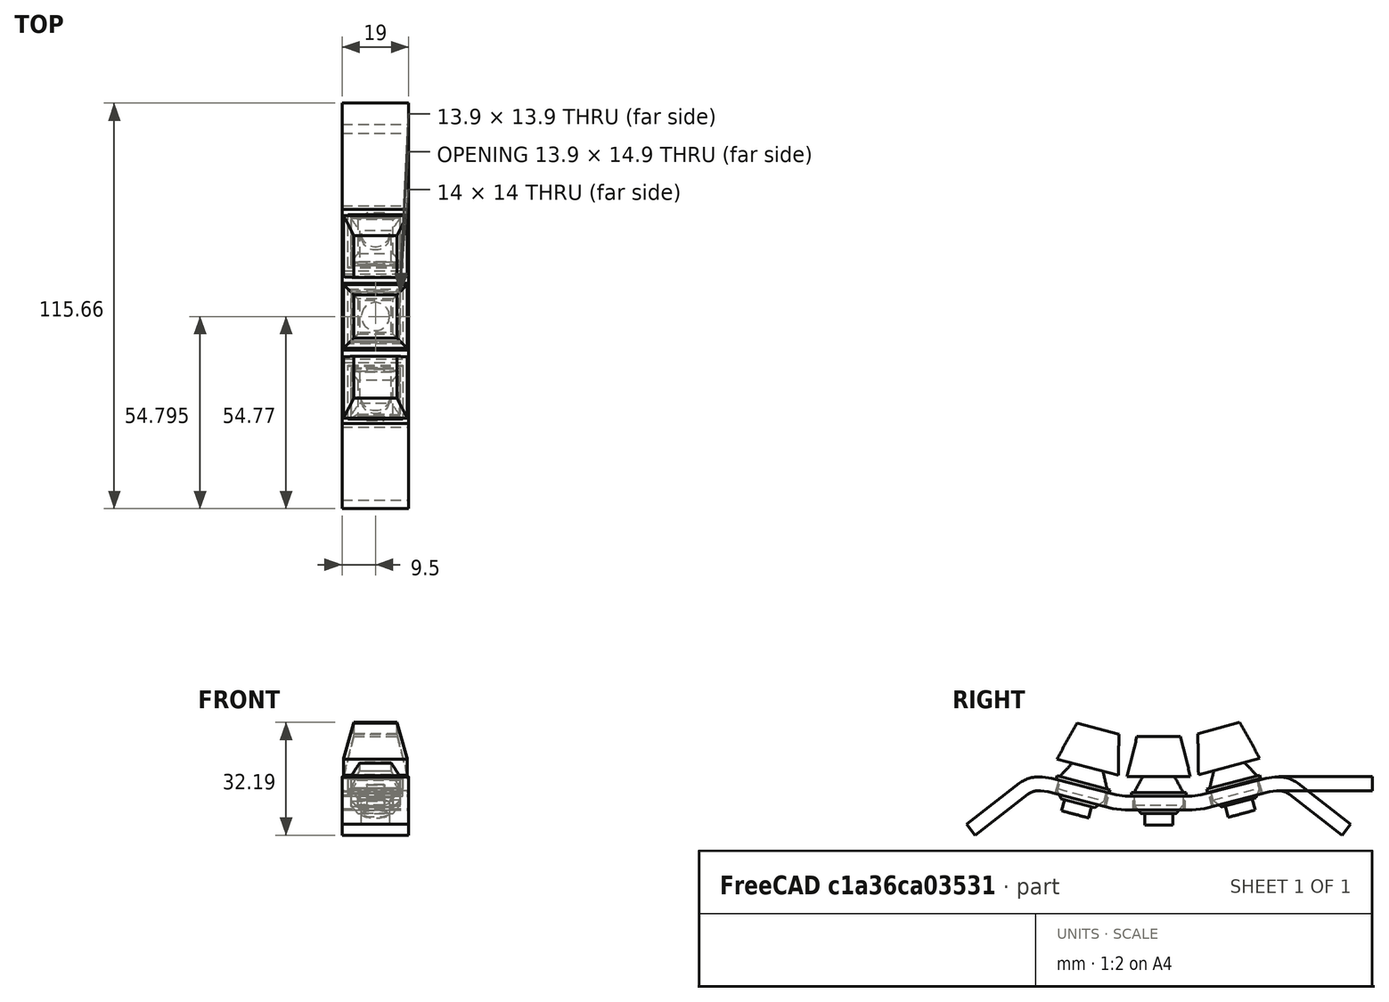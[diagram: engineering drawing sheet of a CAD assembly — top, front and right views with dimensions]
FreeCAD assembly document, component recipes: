
FREECAD ASSEMBLY — COMPONENT RECIPES ("KeyColumn")

This assembly document has 6 components, labeled P0..P5 below (a component is one placed body or linked part). 5 of them carry a construction recipe — the FreeCAD feature program that regenerates the part from scratch, quoted from this document or its linked companion documents; the rest are supplied as boundary geometry only. No exploded tour is included for this assembly.
COMPONENT P0 — recipe-attached ("KeyColumnBase", modeled in this document).
Construction recipe (the document's own serialized feature program — sketch geometry with constraints, then the solid features built on it; lengths are millimeters unless a unit is written):

FEATURE [Sketcher::SketchObject] Sketch
  FullyConstrained = true
  MapMode = 5
  Placement = pos=(0,0,0) rot=(0.57735,0.57735,0.57735;2.0944rad)
  Support = -> [YZ_Plane]
  expr: Constraints[12] = 180 - 7.25
  expr: Constraints[13] = 180 - 7.25
  expr: Constraints[16] = 180 - 7.25
  expr: Constraints[18] = 180 - 7.25
  expr: Constraints[22] = 180 - 7.25
  expr: Constraints[6] = 19.05 mm / 2
  expr: Constraints[7] = 19.05 mm / 2
  expr: Constraints[9] = 180 - 7.25
  sketch-geometry (35):
    g0: LineSegment StartX=-9.525 StartY=2 StartZ=0 EndX=9.525 EndY=2 EndZ=0
    g1: LineSegment StartX=9.525 StartY=2 StartZ=0 EndX=12.1042 EndY=2.32812 EndZ=0
    g2: LineSegment StartX=12.1042 StartY=2.32812 StartZ=0 EndX=30.5474 EndY=7.09786 EndZ=0
    g3: LineSegment StartX=30.5474 StartY=7.09786 StartZ=0 EndX=33.1266 EndY=7.42597 EndZ=0
    g4: LineSegment StartX=-9.525 StartY=2 StartZ=0 EndX=-12.1042 EndY=2.32812 EndZ=0
    g5: LineSegment StartX=-12.1042 StartY=2.32812 StartZ=0 EndX=-30.5474 EndY=7.09786 EndZ=0
    g6: ArcOfCircle CenterX=34.2584 CenterY=-1.47035 CenterZ=0 NormalX=0 NormalY=0 NormalZ=1 AngleXU=0 Radius=8.96802 StartAngle=0.911935 EndAngle=1.69733
    g7: LineSegment StartX=-30.5474 StartY=7.09786 StartZ=0 EndX=-33.1266 EndY=7.42597 EndZ=0
    g8: ArcOfCircle CenterX=-34.2584 CenterY=-1.47035 CenterZ=0 NormalX=0 NormalY=0 NormalZ=1 AngleXU=0 Radius=8.96802 StartAngle=1.44426 EndAngle=2.22966
    g9: LineSegment StartX=-31.5489 StartY=3.22527 StartZ=0 EndX=-13.1057 EndY=-1.54447 EndZ=0
    g10: LineSegment StartX=-9.525 StartY=-2 StartZ=0 EndX=9.525 EndY=-2 EndZ=0
    g11: LineSegment StartX=13.1057 StartY=-1.54447 StartZ=0 EndX=31.5489 EndY=3.22527 EndZ=0
    g12: LineSegment StartX=12.1042 StartY=2.32812 StartZ=0 EndX=13.1057 EndY=-1.54447 EndZ=0
    g13: LineSegment StartX=-13.1057 StartY=-1.54447 StartZ=0 EndX=-12.1042 EndY=2.32812 EndZ=0
    g14: LineSegment StartX=-13.1057 StartY=-1.54447 StartZ=0 EndX=-9.525 EndY=-2 EndZ=0
    g15: LineSegment StartX=9.525 StartY=-2 StartZ=0 EndX=13.1057 EndY=-1.54447 EndZ=0
    g16: LineSegment StartX=9.525 StartY=2 StartZ=0 EndX=9.525 EndY=-2 EndZ=0
    g17: LineSegment StartX=-33.1266 StartY=7.42597 StartZ=0 EndX=-33.6274 EndY=3.48968 EndZ=0
    g18: LineSegment StartX=-31.5489 StartY=3.22527 StartZ=0 EndX=-33.6274 EndY=3.48968 EndZ=0
    g19: LineSegment StartX=33.1266 StartY=7.42597 StartZ=0 EndX=33.6274 EndY=3.48968 EndZ=0
    g20: LineSegment StartX=31.5489 StartY=3.22527 StartZ=0 EndX=33.6274 EndY=3.48968 EndZ=0
    g21: ArcOfCircle CenterX=34.2584 CenterY=-1.47035 CenterZ=0 NormalX=0 NormalY=0 NormalZ=1 AngleXU=0 Radius=5 StartAngle=0.911935 EndAngle=1.69733
    g22: ArcOfCircle CenterX=-34.2584 CenterY=-1.47035 CenterZ=0 NormalX=0 NormalY=0 NormalZ=1 AngleXU=0 Radius=5 StartAngle=1.44426 EndAngle=2.22966
    g23: LineSegment StartX=-39.7488 StartY=5.62057 StartZ=0 EndX=-37.3195 EndY=2.4831 EndZ=0
    g24: LineSegment StartX=37.3195 StartY=2.4831 StartZ=0 EndX=39.7488 EndY=5.62057 EndZ=0
    g25: LineSegment StartX=33.6274 StartY=3.48968 StartZ=0 EndX=34.2584 EndY=-1.47035 EndZ=0
    g26: LineSegment StartX=37.3195 StartY=2.4831 StartZ=0 EndX=34.2584 EndY=-1.47035 EndZ=0
    g27: LineSegment StartX=-33.6274 StartY=3.48968 StartZ=0 EndX=-34.2584 EndY=-1.47035 EndZ=0
    g28: LineSegment StartX=-37.3195 StartY=2.4831 StartZ=0 EndX=-34.2584 EndY=-1.47035 EndZ=0
    g29: LineSegment StartX=37.3195 StartY=2.4831 StartZ=0 EndX=52.3426 EndY=-9.14903 EndZ=0
    g30: LineSegment StartX=52.3426 StartY=-9.14903 StartZ=0 EndX=54.7719 EndY=-6.01155 EndZ=0
    g31: LineSegment StartX=54.7719 StartY=-6.01155 StartZ=0 EndX=39.7488 EndY=5.62057 EndZ=0
    g32: LineSegment StartX=-39.7488 StartY=5.62057 StartZ=0 EndX=-54.7719 EndY=-6.01155 EndZ=0
    g33: LineSegment StartX=-54.7719 StartY=-6.01155 StartZ=0 EndX=-52.3426 EndY=-9.14903 EndZ=0
    g34: LineSegment StartX=-52.3426 StartY=-9.14903 StartZ=0 EndX=-37.3195 EndY=2.4831 EndZ=0
  constraints (94):
    c: Horizontal(g0)
    c: Coincident(g1,g0)
    c: Coincident(g3,g2)
    c: Coincident(g4,g0)
    c: Coincident(g5,g4)
    c: DistanceY(g-1,g0) = 2
    c: DistanceX(g-1,g0) = 9.525
    c: DistanceX(g0,g-1) = 9.525
    c: Distance(g1) = 2.6
    c: Angle(g1,g0) = 3.01506
    c: Coincident(g2,g1)
    c: Distance(g2) = 19.05
    c: Angle(g2,g1) = 3.01506
    c: Angle(g0,g4) = 3.01506
    c: Distance(g4) = 2.6
    c: Distance(g5) = 19.05
    c: Angle(g4,g5) = 3.01506
    c: Distance(g3) = 2.6
    c: Angle(g2,g3) = 3.01506
    c: Coincident(g6,g3)
    c: Coincident(g7,g5)
    c: Distance(g7) = 2.6
    c: Angle(g7,g5) = 3.01506
    c: Coincident(g8,g7)
    c: Horizontal(g10)
    c: Parallel(g2,g11)
    c: Parallel(g9,g5)
    c: Equal(g5,g9)
    c: Equal(g0,g10)
    c: Equal(g2,g11)
    c: Distance(g0,g10) = 4
    c: Coincident(g12,g1)
    c: Coincident(g12,g11)
    c: Perpendicular(g11,g12)
    c: Distance(g12) = 4
    c: Coincident(g13,g9)
    c: Coincident(g13,g4)
    c: Perpendicular(g9,g13)
    c: Distance(g13) = 4
    c: Coincident(g14,g9)
    c: Coincident(g14,g10)
    c: Coincident(g15,g10)
    c: Coincident(g15,g11)
    c: Coincident(g16,g0)
    c: Coincident(g16,g10)
    c: Perpendicular(g10,g16)
    c: Coincident(g17,g7)
    c: Coincident(g18,g9)
    c: Coincident(g18,g17)
    c: Perpendicular(g18,g17)
    c: Parallel(g7,g18)
    c: Coincident(g19,g3)
    c: Coincident(g20,g11)
    c: Coincident(g20,g19)
    c: Parallel(g3,g20)
    c: Perpendicular(g19,g3)
    c: Coincident(g21,g6)
    c: Coincident(g21,g20)
    c: Coincident(g22,g8)
    c: Coincident(g22,g18)
    c: Coincident(g23,g8)
    c: Coincident(g23,g22)
    c: Coincident(g24,g21)
    c: Coincident(g24,g6)
    c: Coincident(g25,g20)
    c: Coincident(g25,g6)
    c: Coincident(g26,g21)
    c: Coincident(g26,g6)
    c: Parallel(g26,g24)
    c: Parallel(g19,g25)
    c: Coincident(g27,g18)
    c: Coincident(g27,g8)
    c: Coincident(g28,g22)
    c: Coincident(g28,g8)
    c: Parallel(g23,g28)
    c: Parallel(g27,g17)
    c: Distance(g28) = 5
    c: Distance(g26) = 5
    c: Angle(g27,g28) = 0.785398
    c: Angle(g26,g25) = 0.785398
    c: Tangent(g21,g29) = 1.5708
    c: Coincident(g29,g30)
    c: Coincident(g30,g31)
    c: Coincident(g31,g6)
    c: Tangent(g8,g32) = -1.5708
    c: Coincident(g32,g33)
    c: Coincident(g33,g34)
    c: Coincident(g34,g22)
    c: Perpendicular(g33,g32)
    c: Perpendicular(g34,g33)
    c: Perpendicular(g29,g30)
    c: Perpendicular(g31,g30)
    c: Distance(g31) = 19
    c: Distance(g32) = 19
FEATURE [PartDesign::Pad] Pad
  Direction = (1,-2e-16,3e-16)
  Length = 19
  Length2 = 10
  Midplane = true
  Placement = pos=(0,0,0) rot=(1,1,1;2.0944rad)
  Profile = -> Sketch
  ReferenceAxis = -> Sketch [N_Axis]
  Type = 0
FEATURE [PartDesign::Body] Body  label="KeyColumnBase"
  Group = -> [Sketch,Pad]
  Origin = -> Origin
  Tip = -> Pad
COMPONENT P1 — recipe-attached ("SubtractorTop", modeled in this document).
Construction recipe (the document's own serialized feature program — sketch geometry with constraints, then the solid features built on it; lengths are millimeters unless a unit is written):

FEATURE [Sketcher::SketchObject] Sketch001
  FullyConstrained = true
  MapMode = 5
  Placement = pos=(0.025,21.3016,4.70673) rot=(0.125206,0.125206,-0.984199;1.58672rad)
  Support = -> [Local_CS]
  sketch-geometry (4):
    g0: LineSegment StartX=-6.95 StartY=6.95 StartZ=0 EndX=6.95 EndY=6.95 EndZ=0
    g1: LineSegment StartX=6.95 StartY=6.95 StartZ=0 EndX=6.95 EndY=-6.95 EndZ=0
    g2: LineSegment StartX=6.95 StartY=-6.95 StartZ=0 EndX=-6.95 EndY=-6.95 EndZ=0
    g3: LineSegment StartX=-6.95 StartY=-6.95 StartZ=0 EndX=-6.95 EndY=6.95 EndZ=0
  constraints (11):
    c: Coincident(g0,g1)
    c: Coincident(g1,g2)
    c: Coincident(g2,g3)
    c: Coincident(g3,g0)
    c: Horizontal(g0)
    c: Horizontal(g2)
    c: Vertical(g1)
    c: Vertical(g3)
    c: Symmetric(g0,g1,g-1)
    c: Equal(g0,g3)
    c: DistanceX(g0,g0) = 13.9
FEATURE [PartDesign::Pad] Pad001
  Direction = (-5e-16,-0.25038,0.968148)
  Length = 10
  Length2 = 10
  Placement = pos=(0.025,21.3016,4.70673) rot=(0.125206,0.125206,-0.984199;1.58672rad)
  Profile = -> Sketch001
  ReferenceAxis = -> Sketch001 [N_Axis]
  Type = 0
FEATURE [Sketcher::SketchObject] Sketch002
  ExternalGeometry = -> [Pad001]
  FullyConstrained = true
  MapMode = 5
  Placement = pos=(0.025,21.3016,4.70673) rot=(-0.704263,0.704263,0.089594;2.96288rad)
  Support = -> [Pad001]
  sketch-geometry (4):
    g0: LineSegment StartX=-6.95 StartY=6.95 StartZ=0 EndX=6.95 EndY=6.95 EndZ=0
    g1: LineSegment StartX=6.95 StartY=6.95 StartZ=0 EndX=6.95 EndY=-6.95 EndZ=0
    g2: LineSegment StartX=6.95 StartY=-6.95 StartZ=0 EndX=-6.95 EndY=-6.95 EndZ=0
    g3: LineSegment StartX=-6.95 StartY=-6.95 StartZ=0 EndX=-6.95 EndY=6.95 EndZ=0
  constraints (10):
    c: Coincident(g0,g1)
    c: Coincident(g1,g2)
    c: Coincident(g2,g3)
    c: Coincident(g3,g0)
    c: Horizontal(g0)
    c: Horizontal(g2)
    c: Vertical(g1)
    c: Vertical(g3)
    c: Coincident(g0,g-3)
    c: Coincident(g1,g-4)
FEATURE [PartDesign::Pad] Pad002
  BaseFeature = -> Pad001
  Direction = (4e-16,0.25038,-0.968148)
  Length = 1.3
  Length2 = 10
  Placement = pos=(0.025,21.3016,4.70673) rot=(0.125206,0.125206,-0.984199;1.58672rad)
  Profile = -> Sketch002
  ReferenceAxis = -> Sketch002 [N_Axis]
  Type = 0
FEATURE [Sketcher::SketchObject] Sketch003
  ExternalGeometry = -> [Pad002]
  FullyConstrained = true
  MapMode = 5
  Placement = pos=(0.025,21.6271,3.44814) rot=(-0.704263,0.704263,0.089594;2.96288rad)
  Support = -> [Pad002]
  sketch-geometry (12):
    g0: LineSegment StartX=-6.95 StartY=6.95 StartZ=0 EndX=-6.95 EndY=2.5 EndZ=0
    g1: LineSegment StartX=-6.95 StartY=2.5 StartZ=0 EndX=-7.45 EndY=2.5 EndZ=0
    g2: LineSegment StartX=-7.45 StartY=2.5 StartZ=0 EndX=-7.45 EndY=-2.5 EndZ=0
    g3: LineSegment StartX=-7.45 StartY=-2.5 StartZ=0 EndX=-6.95 EndY=-2.5 EndZ=0
    g4: LineSegment StartX=-6.95 StartY=-2.5 StartZ=0 EndX=-6.95 EndY=-6.95 EndZ=0
    g5: LineSegment StartX=-6.95 StartY=-6.95 StartZ=0 EndX=6.95 EndY=-6.95 EndZ=0
    g6: LineSegment StartX=6.95 StartY=-6.95 StartZ=0 EndX=6.95 EndY=-2.5 EndZ=0
    g7: LineSegment StartX=6.95 StartY=-2.5 StartZ=0 EndX=7.45 EndY=-2.5 EndZ=0
    g8: LineSegment StartX=7.45 StartY=-2.5 StartZ=0 EndX=7.45 EndY=2.5 EndZ=0
    g9: LineSegment StartX=7.45 StartY=2.5 StartZ=0 EndX=6.95 EndY=2.5 EndZ=0
    g10: LineSegment StartX=6.95 StartY=2.5 StartZ=0 EndX=6.95 EndY=6.95 EndZ=0
    g11: LineSegment StartX=6.95 StartY=6.95 StartZ=0 EndX=-6.95 EndY=6.95 EndZ=0
  constraints (33):
    c: Coincident(g0,g-3)
    c: Vertical(g0)
    c: Coincident(g0,g1)
    c: Horizontal(g1)
    c: Coincident(g1,g2)
    c: Vertical(g2)
    c: Coincident(g2,g3)
    c: Coincident(g3,g4)
    c: Vertical(g4)
    c: Coincident(g4,g5)
    c: Coincident(g5,g-4)
    c: Horizontal(g5)
    c: Coincident(g5,g6)
    c: Vertical(g6)
    c: Coincident(g6,g7)
    c: Coincident(g7,g8)
    c: Vertical(g8)
    c: Coincident(g8,g9)
    c: Coincident(g9,g10)
    c: Vertical(g10)
    c: Coincident(g10,g11)
    c: Coincident(g11,g0)
    c: Horizontal(g11)
    c: Horizontal(g3)
    c: Horizontal(g7)
    c: Horizontal(g9)
    c: Vertical(g9,g6)
    c: DistanceX(g3,g3) = 0.5
    c: Equal(g3,g7)
    c: DistanceY(g8,g8) = 5
    c: Symmetric(g2,g8,g-1)
    c: Equal(g8,g2)
    c: Horizontal(g3,g6)
FEATURE [PartDesign::Pad] Pad003
  BaseFeature = -> Pad002
  Direction = (4e-16,0.25038,-0.968148)
  Length = 2.7
  Length2 = 10
  Placement = pos=(0.025,21.3016,4.70673) rot=(0.125206,0.125206,-0.984199;1.58672rad)
  Profile = -> Sketch003
  ReferenceAxis = -> Sketch003 [N_Axis]
  Type = 0
FEATURE [PartDesign::Pad] Pad004
  BaseFeature = -> Pad003
  Direction = (4e-16,0.25038,-0.968148)
  Length = 10
  Length2 = 10
  Placement = pos=(0.025,21.3016,4.70673) rot=(0.125206,0.125206,-0.984199;1.58672rad)
  Profile = -> Sketch003
  ReferenceAxis = -> Sketch003 [N_Axis]
  Type = 0
FEATURE [PartDesign::Body] Body001  label="SubtractorTop"
  Group = -> [Sketch001,Pad001,Sketch002,Pad002,Sketch003,Pad003,Pad004]
  Origin = -> Origin001
  Tip = -> Pad004
COMPONENT P2 — recipe-attached ("SubtractorMiddle", modeled in this document).
Construction recipe (the document's own serialized feature program — sketch geometry with constraints, then the solid features built on it; lengths are millimeters unless a unit is written):

FEATURE [Sketcher::SketchObject] Sketch005
  FullyConstrained = true
  MapMode = 5
  Placement = pos=(0,0.025,2) rot=(0,0,-1;1.5708rad)
  Support = -> [Local_CS002]
  sketch-geometry (4):
    g0: LineSegment StartX=-6.95 StartY=6.95 StartZ=0 EndX=6.95 EndY=6.95 EndZ=0
    g1: LineSegment StartX=6.95 StartY=6.95 StartZ=0 EndX=6.95 EndY=-6.95 EndZ=0
    g2: LineSegment StartX=6.95 StartY=-6.95 StartZ=0 EndX=-6.95 EndY=-6.95 EndZ=0
    g3: LineSegment StartX=-6.95 StartY=-6.95 StartZ=0 EndX=-6.95 EndY=6.95 EndZ=0
  constraints (11):
    c: Coincident(g0,g1)
    c: Coincident(g1,g2)
    c: Coincident(g2,g3)
    c: Coincident(g3,g0)
    c: Horizontal(g0)
    c: Horizontal(g2)
    c: Vertical(g1)
    c: Vertical(g3)
    c: Symmetric(g0,g1,g-1)
    c: Equal(g0,g3)
    c: DistanceX(g0,g0) = 13.9
FEATURE [PartDesign::Pad] Pad006
  Direction = (-4e-16,6e-16,1)
  Length = 10
  Length2 = 10
  Placement = pos=(0,0.025,2) rot=(0,0,-1;1.5708rad)
  Profile = -> Sketch005
  ReferenceAxis = -> Sketch005 [N_Axis]
  Type = 0
FEATURE [Sketcher::SketchObject] Sketch006
  ExternalGeometry = -> [Pad006]
  FullyConstrained = true
  MapMode = 5
  Placement = pos=(0,0.025,2) rot=(-0.707107,0.707107,0;3.14159rad)
  Support = -> [Pad006]
  sketch-geometry (4):
    g0: LineSegment StartX=-6.95 StartY=6.95 StartZ=0 EndX=6.95 EndY=6.95 EndZ=0
    g1: LineSegment StartX=6.95 StartY=6.95 StartZ=0 EndX=6.95 EndY=-6.95 EndZ=0
    g2: LineSegment StartX=6.95 StartY=-6.95 StartZ=0 EndX=-6.95 EndY=-6.95 EndZ=0
    g3: LineSegment StartX=-6.95 StartY=-6.95 StartZ=0 EndX=-6.95 EndY=6.95 EndZ=0
  constraints (10):
    c: Coincident(g0,g1)
    c: Coincident(g1,g2)
    c: Coincident(g2,g3)
    c: Coincident(g3,g0)
    c: Horizontal(g0)
    c: Horizontal(g2)
    c: Vertical(g1)
    c: Vertical(g3)
    c: Coincident(g0,g-3)
    c: Coincident(g1,g-4)
FEATURE [PartDesign::Pad] Pad007
  BaseFeature = -> Pad006
  Direction = (4e-16,-6e-16,-1)
  Length = 1.3
  Length2 = 10
  Placement = pos=(0,0.025,2) rot=(0,0,-1;1.5708rad)
  Profile = -> Sketch006
  ReferenceAxis = -> Sketch006 [N_Axis]
  Type = 0
FEATURE [Sketcher::SketchObject] Sketch007
  ExternalGeometry = -> [Pad007]
  FullyConstrained = true
  MapMode = 5
  Placement = pos=(5e-16,0.025,0.7) rot=(-0.707107,0.707107,0;3.14159rad)
  Support = -> [Pad007]
  sketch-geometry (12):
    g0: LineSegment StartX=-6.95 StartY=6.95 StartZ=0 EndX=-6.95 EndY=2.5 EndZ=0
    g1: LineSegment StartX=-6.95 StartY=2.5 StartZ=0 EndX=-7.45 EndY=2.5 EndZ=0
    g2: LineSegment StartX=-7.45 StartY=2.5 StartZ=0 EndX=-7.45 EndY=-2.5 EndZ=0
    g3: LineSegment StartX=-7.45 StartY=-2.5 StartZ=0 EndX=-6.95 EndY=-2.5 EndZ=0
    g4: LineSegment StartX=-6.95 StartY=-2.5 StartZ=0 EndX=-6.95 EndY=-6.95 EndZ=0
    g5: LineSegment StartX=-6.95 StartY=-6.95 StartZ=0 EndX=6.95 EndY=-6.95 EndZ=0
    g6: LineSegment StartX=6.95 StartY=-6.95 StartZ=0 EndX=6.95 EndY=-2.5 EndZ=0
    g7: LineSegment StartX=6.95 StartY=-2.5 StartZ=0 EndX=7.45 EndY=-2.5 EndZ=0
    g8: LineSegment StartX=7.45 StartY=-2.5 StartZ=0 EndX=7.45 EndY=2.5 EndZ=0
    g9: LineSegment StartX=7.45 StartY=2.5 StartZ=0 EndX=6.95 EndY=2.5 EndZ=0
    g10: LineSegment StartX=6.95 StartY=2.5 StartZ=0 EndX=6.95 EndY=6.95 EndZ=0
    g11: LineSegment StartX=6.95 StartY=6.95 StartZ=0 EndX=-6.95 EndY=6.95 EndZ=0
  constraints (33):
    c: Coincident(g0,g-3)
    c: Vertical(g0)
    c: Coincident(g0,g1)
    c: Horizontal(g1)
    c: Coincident(g1,g2)
    c: Vertical(g2)
    c: Coincident(g2,g3)
    c: Coincident(g3,g4)
    c: Vertical(g4)
    c: Coincident(g4,g5)
    c: Coincident(g5,g-4)
    c: Horizontal(g5)
    c: Coincident(g5,g6)
    c: Vertical(g6)
    c: Coincident(g6,g7)
    c: Coincident(g7,g8)
    c: Vertical(g8)
    c: Coincident(g8,g9)
    c: Coincident(g9,g10)
    c: Vertical(g10)
    c: Coincident(g10,g11)
    c: Coincident(g11,g0)
    c: Horizontal(g11)
    c: Horizontal(g3)
    c: Horizontal(g7)
    c: Horizontal(g9)
    c: Vertical(g9,g6)
    c: DistanceX(g3,g3) = 0.5
    c: Equal(g3,g7)
    c: DistanceY(g8,g8) = 5
    c: Symmetric(g2,g8,g-1)
    c: Equal(g8,g2)
    c: Horizontal(g3,g6)
FEATURE [PartDesign::Pad] Pad008
  BaseFeature = -> Pad007
  Direction = (4e-16,-6e-16,-1)
  Length = 2.7
  Length2 = 10
  Placement = pos=(0,0.025,2) rot=(0,0,-1;1.5708rad)
  Profile = -> Sketch007
  ReferenceAxis = -> Sketch007 [N_Axis]
  Type = 0
FEATURE [PartDesign::Pad] Pad009
  BaseFeature = -> Pad008
  Direction = (4e-16,-6e-16,-1)
  Length = 10
  Length2 = 10
  Placement = pos=(0,0.025,2) rot=(0,0,-1;1.5708rad)
  Profile = -> Sketch007
  ReferenceAxis = -> Sketch007 [N_Axis]
  Type = 0
FEATURE [PartDesign::Body] Body002  label="SubtractorMiddle"
  Group = -> [Sketch005,Pad006,Sketch006,Pad007,Sketch007,Pad008,Pad009]
  Origin = -> Origin002
  Tip = -> Pad009
COMPONENT P3 — recipe-attached ("SubtractorBottom", modeled in this document).
Construction recipe (the document's own serialized feature program — sketch geometry with constraints, then the solid features built on it; lengths are millimeters unless a unit is written):

FEATURE [Sketcher::SketchObject] Sketch009
  FullyConstrained = true
  MapMode = 5
  Placement = pos=(-5.3e-15,-21.35,4.71925) rot=(-0.125206,-0.125206,-0.984199;1.58672rad)
  Support = -> [Local_CS001]
  sketch-geometry (4):
    g0: LineSegment StartX=-6.95 StartY=6.95 StartZ=0 EndX=6.95 EndY=6.95 EndZ=0
    g1: LineSegment StartX=6.95 StartY=6.95 StartZ=0 EndX=6.95 EndY=-6.95 EndZ=0
    g2: LineSegment StartX=6.95 StartY=-6.95 StartZ=0 EndX=-6.95 EndY=-6.95 EndZ=0
    g3: LineSegment StartX=-6.95 StartY=-6.95 StartZ=0 EndX=-6.95 EndY=6.95 EndZ=0
  constraints (11):
    c: Coincident(g0,g1)
    c: Coincident(g1,g2)
    c: Coincident(g2,g3)
    c: Coincident(g3,g0)
    c: Horizontal(g0)
    c: Horizontal(g2)
    c: Vertical(g1)
    c: Vertical(g3)
    c: Symmetric(g0,g1,g-1)
    c: Equal(g0,g3)
    c: DistanceX(g0,g0) = 13.9
FEATURE [PartDesign::Pad] Pad011
  Direction = (-2e-16,0.25038,0.968148)
  Length = 10
  Length2 = 10
  Placement = pos=(-5.3e-15,-21.35,4.71925) rot=(-0.125206,-0.125206,-0.984199;1.58672rad)
  Profile = -> Sketch009
  ReferenceAxis = -> Sketch009 [N_Axis]
  Type = 0
FEATURE [Sketcher::SketchObject] Sketch010
  ExternalGeometry = -> [Pad011]
  FullyConstrained = true
  MapMode = 5
  Placement = pos=(-5.3e-15,-21.35,4.71925) rot=(-0.704263,0.704263,-0.089594;3.3203rad)
  Support = -> [Pad011]
  sketch-geometry (4):
    g0: LineSegment StartX=-6.95 StartY=6.95 StartZ=0 EndX=6.95 EndY=6.95 EndZ=0
    g1: LineSegment StartX=6.95 StartY=6.95 StartZ=0 EndX=6.95 EndY=-6.95 EndZ=0
    g2: LineSegment StartX=6.95 StartY=-6.95 StartZ=0 EndX=-6.95 EndY=-6.95 EndZ=0
    g3: LineSegment StartX=-6.95 StartY=-6.95 StartZ=0 EndX=-6.95 EndY=6.95 EndZ=0
  constraints (10):
    c: Coincident(g0,g1)
    c: Coincident(g1,g2)
    c: Coincident(g2,g3)
    c: Coincident(g3,g0)
    c: Horizontal(g0)
    c: Horizontal(g2)
    c: Vertical(g1)
    c: Vertical(g3)
    c: Coincident(g0,g-3)
    c: Coincident(g1,g-4)
FEATURE [PartDesign::Pad] Pad012
  BaseFeature = -> Pad011
  Direction = (2e-16,-0.25038,-0.968148)
  Length = 1.3
  Length2 = 10
  Placement = pos=(-5.3e-15,-21.35,4.71925) rot=(-0.125206,-0.125206,-0.984199;1.58672rad)
  Profile = -> Sketch010
  ReferenceAxis = -> Sketch010 [N_Axis]
  Type = 0
FEATURE [Sketcher::SketchObject] Sketch011
  ExternalGeometry = -> [Pad012]
  FullyConstrained = true
  MapMode = 5
  Placement = pos=(-5e-15,-21.6755,3.46065) rot=(-0.704263,0.704263,-0.089594;3.3203rad)
  Support = -> [Pad012]
  sketch-geometry (12):
    g0: LineSegment StartX=-6.95 StartY=6.95 StartZ=0 EndX=-6.95 EndY=2.5 EndZ=0
    g1: LineSegment StartX=-6.95 StartY=2.5 StartZ=0 EndX=-7.45 EndY=2.5 EndZ=0
    g2: LineSegment StartX=-7.45 StartY=2.5 StartZ=0 EndX=-7.45 EndY=-2.5 EndZ=0
    g3: LineSegment StartX=-7.45 StartY=-2.5 StartZ=0 EndX=-6.95 EndY=-2.5 EndZ=0
    g4: LineSegment StartX=-6.95 StartY=-2.5 StartZ=0 EndX=-6.95 EndY=-6.95 EndZ=0
    g5: LineSegment StartX=-6.95 StartY=-6.95 StartZ=0 EndX=6.95 EndY=-6.95 EndZ=0
    g6: LineSegment StartX=6.95 StartY=-6.95 StartZ=0 EndX=6.95 EndY=-2.5 EndZ=0
    g7: LineSegment StartX=6.95 StartY=-2.5 StartZ=0 EndX=7.45 EndY=-2.5 EndZ=0
    g8: LineSegment StartX=7.45 StartY=-2.5 StartZ=0 EndX=7.45 EndY=2.5 EndZ=0
    g9: LineSegment StartX=7.45 StartY=2.5 StartZ=0 EndX=6.95 EndY=2.5 EndZ=0
    g10: LineSegment StartX=6.95 StartY=2.5 StartZ=0 EndX=6.95 EndY=6.95 EndZ=0
    g11: LineSegment StartX=6.95 StartY=6.95 StartZ=0 EndX=-6.95 EndY=6.95 EndZ=0
  constraints (33):
    c: Coincident(g0,g-3)
    c: Vertical(g0)
    c: Coincident(g0,g1)
    c: Horizontal(g1)
    c: Coincident(g1,g2)
    c: Vertical(g2)
    c: Coincident(g2,g3)
    c: Coincident(g3,g4)
    c: Vertical(g4)
    c: Coincident(g4,g5)
    c: Coincident(g5,g-4)
    c: Horizontal(g5)
    c: Coincident(g5,g6)
    c: Vertical(g6)
    c: Coincident(g6,g7)
    c: Coincident(g7,g8)
    c: Vertical(g8)
    c: Coincident(g8,g9)
    c: Coincident(g9,g10)
    c: Vertical(g10)
    c: Coincident(g10,g11)
    c: Coincident(g11,g0)
    c: Horizontal(g11)
    c: Horizontal(g3)
    c: Horizontal(g7)
    c: Horizontal(g9)
    c: Vertical(g9,g6)
    c: DistanceX(g3,g3) = 0.5
    c: Equal(g3,g7)
    c: DistanceY(g8,g8) = 5
    c: Symmetric(g2,g8,g-1)
    c: Equal(g8,g2)
    c: Horizontal(g3,g6)
FEATURE [PartDesign::Pad] Pad013
  BaseFeature = -> Pad012
  Direction = (2e-16,-0.25038,-0.968148)
  Length = 2.7
  Length2 = 10
  Placement = pos=(-5.3e-15,-21.35,4.71925) rot=(-0.125206,-0.125206,-0.984199;1.58672rad)
  Profile = -> Sketch011
  ReferenceAxis = -> Sketch011 [N_Axis]
  Type = 0
FEATURE [PartDesign::Pad] Pad014
  BaseFeature = -> Pad013
  Direction = (2e-16,-0.25038,-0.968148)
  Length = 10
  Length2 = 10
  Placement = pos=(-5.3e-15,-21.35,4.71925) rot=(-0.125206,-0.125206,-0.984199;1.58672rad)
  Profile = -> Sketch011
  ReferenceAxis = -> Sketch011 [N_Axis]
  Type = 0
FEATURE [PartDesign::Body] Body003  label="SubtractorBottom"
  Group = -> [Sketch009,Pad011,Sketch010,Pad012,Sketch011,Pad013,Pad014]
  Origin = -> Origin003
  Tip = -> Pad014
COMPONENT P4 — recipe-attached ("KeyColumnStraightBase", modeled in this document).
Construction recipe (the document's own serialized feature program — sketch geometry with constraints, then the solid features built on it; lengths are millimeters unless a unit is written):

FEATURE [Sketcher::SketchObject] Sketch012
  FullyConstrained = true
  MapMode = 5
  Placement = pos=(0,0,0) rot=(0.57735,0.57735,0.57735;2.0944rad)
  Support = -> [YZ_Plane005]
  expr: Constraints[12] = 180 - 7.25
  expr: Constraints[13] = 180 - 7.25
  expr: Constraints[16] = 180 - 7.25
  expr: Constraints[19] = 180 - 7.25
  expr: Constraints[6] = 19.05 mm / 2
  expr: Constraints[74] = 172.75
  expr: Constraints[7] = 19.05 mm / 2
  expr: Constraints[9] = 180 - 7.25
  sketch-geometry (32):
    g0: LineSegment StartX=-9.525 StartY=2 StartZ=0 EndX=9.525 EndY=2 EndZ=0
    g1: LineSegment StartX=9.525 StartY=2 StartZ=0 EndX=12.1042 EndY=2.32812 EndZ=0
    g2: LineSegment StartX=12.1042 StartY=2.32812 StartZ=0 EndX=30.5474 EndY=7.09786 EndZ=0
    g3: LineSegment StartX=30.5474 StartY=7.09786 StartZ=0 EndX=33.1266 EndY=7.42597 EndZ=0
    g4: LineSegment StartX=-9.525 StartY=2 StartZ=0 EndX=-12.1042 EndY=2.32812 EndZ=0
    g5: LineSegment StartX=-12.1042 StartY=2.32812 StartZ=0 EndX=-30.5474 EndY=7.09786 EndZ=0
    g6: LineSegment StartX=-30.5474 StartY=7.09786 StartZ=0 EndX=-33.1266 EndY=7.42597 EndZ=0
    g7: ArcOfCircle CenterX=-34.2584 CenterY=-1.47035 CenterZ=0 NormalX=0 NormalY=0 NormalZ=1 AngleXU=0 Radius=8.96802 StartAngle=1.44426 EndAngle=2.22966
    g8: LineSegment StartX=-31.5489 StartY=3.22527 StartZ=0 EndX=-13.1057 EndY=-1.54447 EndZ=0
    g9: LineSegment StartX=-9.525 StartY=-2 StartZ=0 EndX=9.525 EndY=-2 EndZ=0
    g10: LineSegment StartX=13.1057 StartY=-1.54447 StartZ=0 EndX=31.5489 EndY=3.22527 EndZ=0
    g11: LineSegment StartX=12.1042 StartY=2.32812 StartZ=0 EndX=13.1057 EndY=-1.54447 EndZ=0
    g12: LineSegment StartX=-13.1057 StartY=-1.54447 StartZ=0 EndX=-12.1042 EndY=2.32812 EndZ=0
    g13: LineSegment StartX=-13.1057 StartY=-1.54447 StartZ=0 EndX=-9.525 EndY=-2 EndZ=0
    g14: LineSegment StartX=9.525 StartY=-2 StartZ=0 EndX=13.1057 EndY=-1.54447 EndZ=0
    g15: LineSegment StartX=9.525 StartY=2 StartZ=0 EndX=9.525 EndY=-2 EndZ=0
    g16: LineSegment StartX=-33.1266 StartY=7.42597 StartZ=0 EndX=-33.6274 EndY=3.48968 EndZ=0
    g17: LineSegment StartX=-31.5489 StartY=3.22527 StartZ=0 EndX=-33.6274 EndY=3.48968 EndZ=0
    g18: LineSegment StartX=31.5489 StartY=3.22527 StartZ=0 EndX=33.6274 EndY=3.48968 EndZ=0
    g19: ArcOfCircle CenterX=-34.2584 CenterY=-1.47035 CenterZ=0 NormalX=0 NormalY=0 NormalZ=1 AngleXU=0 Radius=5 StartAngle=1.44426 EndAngle=2.22966
    g20: LineSegment StartX=-39.7488 StartY=5.62057 StartZ=0 EndX=-37.3195 EndY=2.4831 EndZ=0
    g21: LineSegment StartX=-33.6274 StartY=3.48968 StartZ=0 EndX=-34.2584 EndY=-1.47035 EndZ=0
    g22: LineSegment StartX=-37.3195 StartY=2.4831 StartZ=0 EndX=-34.2584 EndY=-1.47035 EndZ=0
    g23: LineSegment StartX=-39.7488 StartY=5.62057 StartZ=0 EndX=-54.7719 EndY=-6.01155 EndZ=0
    g24: LineSegment StartX=-54.7719 StartY=-6.01155 StartZ=0 EndX=-52.3426 EndY=-9.14903 EndZ=0
    g25: LineSegment StartX=-52.3426 StartY=-9.14903 StartZ=0 EndX=-37.3195 EndY=2.4831 EndZ=0
    g26: LineSegment StartX=34.8894 StartY=3.56963 StartZ=0 EndX=60.8894 EndY=3.56963 EndZ=0
    g27: LineSegment StartX=60.8894 StartY=3.56963 StartZ=0 EndX=60.8894 EndY=7.53765 EndZ=0
    g28: LineSegment StartX=60.8894 StartY=7.53765 StartZ=0 EndX=34.8894 EndY=7.53765 EndZ=0
    g29: ArcOfCircle CenterX=34.8894 CenterY=-6.43037 CenterZ=0 NormalX=0 NormalY=0 NormalZ=1 AngleXU=0 Radius=13.968 StartAngle=1.5708 EndAngle=1.69733
    g30: ArcOfCircle CenterX=34.8894 CenterY=-6.43037 CenterZ=0 NormalX=0 NormalY=0 NormalZ=1 AngleXU=0 Radius=10 StartAngle=1.5708 EndAngle=1.69733
    g31: LineSegment StartX=34.8894 StartY=3.56963 StartZ=0 EndX=34.8894 EndY=-6.43037 EndZ=0
  constraints (85):
    c: Horizontal(g0)
    c: Coincident(g1,g0)
    c: Coincident(g3,g2)
    c: Coincident(g4,g0)
    c: Coincident(g5,g4)
    c: DistanceY(g-1,g0) = 2
    c: DistanceX(g-1,g0) = 9.525
    c: DistanceX(g0,g-1) = 9.525
    c: Distance(g1) = 2.6
    c: Angle(g1,g0) = 3.01506
    c: Coincident(g2,g1)
    c: Distance(g2) = 19.05
    c: Angle(g2,g1) = 3.01506
    c: Angle(g0,g4) = 3.01506
    c: Distance(g4) = 2.6
    c: Distance(g5) = 19.05
    c: Angle(g4,g5) = 3.01506
    c: Coincident(g6,g5)
    c: Distance(g6) = 2.6
    c: Angle(g6,g5) = 3.01506
    c: Coincident(g7,g6)
    c: Horizontal(g9)
    c: Parallel(g2,g10)
    c: Parallel(g8,g5)
    c: Equal(g5,g8)
    c: Equal(g0,g9)
    c: Equal(g2,g10)
    c: Distance(g0,g9) = 4
    c: Coincident(g11,g1)
    c: Coincident(g11,g10)
    c: Perpendicular(g10,g11)
    c: Distance(g11) = 4
    c: Coincident(g12,g8)
    c: Coincident(g12,g4)
    c: Perpendicular(g8,g12)
    c: Distance(g12) = 4
    c: Coincident(g13,g8)
    c: Coincident(g13,g9)
    c: Coincident(g14,g9)
    c: Coincident(g14,g10)
    c: Coincident(g15,g0)
    c: Coincident(g15,g9)
    c: Perpendicular(g9,g15)
    c: Coincident(g16,g6)
    c: Coincident(g17,g8)
    c: Coincident(g17,g16)
    c: Perpendicular(g17,g16)
    c: Parallel(g6,g17)
    c: Coincident(g18,g10)
    c: Parallel(g3,g18)
    c: Coincident(g19,g7)
    c: Coincident(g19,g17)
    c: Coincident(g20,g7)
    c: Coincident(g20,g19)
    c: Coincident(g21,g17)
    c: Coincident(g21,g7)
    c: Coincident(g22,g19)
    c: Coincident(g22,g7)
    c: Parallel(g20,g22)
    c: Parallel(g21,g16)
    c: Distance(g22) = 5
    c: Angle(g21,g22) = 0.785398
    c: Tangent(g7,g23) = -1.5708
    c: Coincident(g23,g24)
    c: Coincident(g24,g25)
    c: Coincident(g25,g19)
    c: Perpendicular(g24,g23)
    c: Perpendicular(g25,g24)
    c: Distance(g23) = 19
    c: Angle(g10,g18) = 3.01506
    c: Coincident(g26,g27)
    c: Coincident(g27,g28)
    c: Parallel(g28,g26)
    c: Perpendicular(g26,g27)
    c: Angle(g18,g26) = 3.01506
    c: Tangent(g3,g29) = 1.5708
    c: Tangent(g28,g29) = -1.5708
    c: Tangent(g26,g30) = 1.5708
    c: Tangent(g18,g30) = 1.5708
    c: Distance(g3) = 2.6
    c: Distance(g28) = 26
    c: Coincident(g30,g29)
    c: Coincident(g31,g26)
    c: Coincident(g31,g29)
    c: Distance(g31) = 10
FEATURE [PartDesign::Pad] Pad015
  Direction = (1,-2e-16,3e-16)
  Length = 19
  Length2 = 10
  Midplane = true
  Placement = pos=(0,0,0) rot=(0.57735,0.57735,0.57735;2.0944rad)
  Profile = -> Sketch012
  ReferenceAxis = -> Sketch012 [N_Axis]
  Type = 0
FEATURE [PartDesign::Body] Body006  label="KeyColumnStraightBase"
  Group = -> [Sketch012,Pad015]
  Origin = -> Origin004
  Tip = -> Pad015
COMPONENT P5 — geometry summary ("MXSwitch100Nice002"; no construction recipe available for this part):
  bounding box: 27.1 x 18.1 x 17.9 mm
  tessellated surface: 588 triangles
  volume: 4560 mm^3 (52% of its bounding box)
  symmetry: mirror-symmetric across its x mid-plane
PROVENANCE & LICENSES
A FreeCAD (.FCStd) document from a public repository crawl; recipes are the document's own serialized feature recipes (and, for linked parts, companion documents' recipes).
License: mit.
